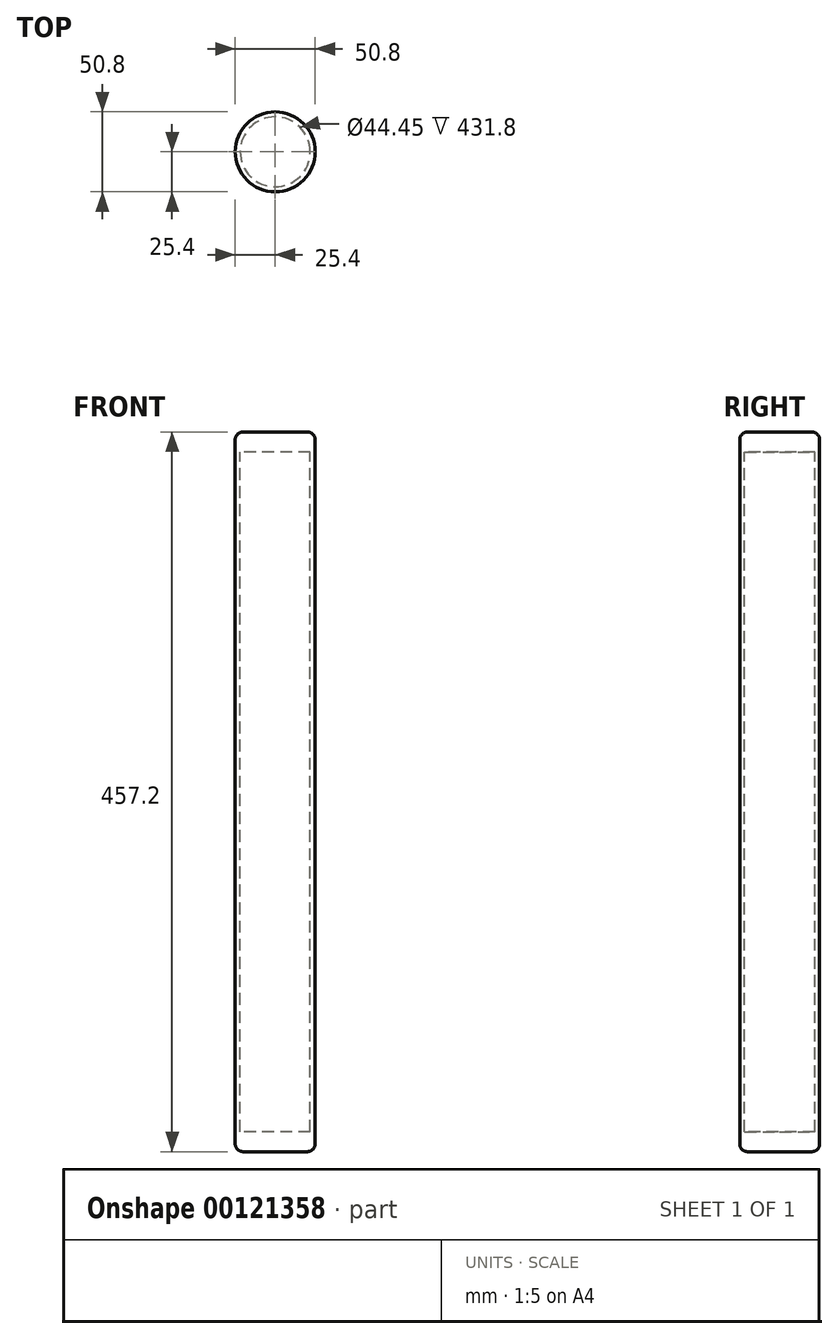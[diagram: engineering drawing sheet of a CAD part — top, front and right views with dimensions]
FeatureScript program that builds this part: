
annotation { "Feature Type Name" : "Feature", "Feature Type Description" : "" }
export const myFeature = defineFeature(function(context is Context, id is Id, definition is map)
    precondition{}
    {
        {
            var Q0;
            Q0=qCreatedBy(makeId("Top.planeOp"),FACE);
            var sketch = newSketch(context, id + "F0", { "sketchPlane" : qUnion([Q0])});
            skCircle(sketch, "E0", {"center": v(0, 0) * mm, "radius": 25.4 * mm});
            skSolve(sketch);
        }
        {
            var Q0;
            Q0 = qSketchRegion(id + "F0", true);
            extrude(context, id + "F1", {"entities" : qUnion([Q0]), "depth" : 444.5 * mm});
        }
        {
            var Q0;
            Q0=makeQuery(id+"F1.opExtrude","CAP_FACE",FACE,{"disambiguationData":[OSD([sQuery(id+"F0.wireOp",EDGE,"E0")])],"isStart":false});
            var sketch = newSketch(context, id + "F2", { "sketchPlane" : qUnion([Q0])});
            skCircle(sketch, "E1", {"center": v(0, 0) * mm, "radius": 22.23 * mm});
            skSolve(sketch);
        }
        {
            var Q0;
            Q0 = qSketchRegion(id + "F2", true);
            extrude(context, id + "F3", {"entities" : qUnion([Q0]), "operationType" : NewBodyOperationType.REMOVE, "oppositeDirection" : true, "depth" : 431.8 * mm});
        }
        {
            var Q0;
            Q0=makeQuery(id+"F1.opExtrude","CAP_FACE",FACE,{"disambiguationData":[OSD([sQuery(id+"F0.wireOp",EDGE,"E0")])],"isStart":false});
            var sketch = newSketch(context, id + "F4", { "sketchPlane" : qUnion([Q0])});
            skCircle(sketch, "E2", {"center": v(0, 0) * mm, "radius": 25.4 * mm});
            skSolve(sketch);
        }
        {
            var Q0;
            Q0 = qSketchRegion(id + "F4", true);
            extrude(context, id + "F5", {"entities" : qUnion([Q0]), "operationType" : NewBodyOperationType.ADD, "depth" : 12.7 * mm});
        }
        {
            var Q0;
            Q0=makeQuery(id+"F5.opExtrude","CAP_EDGE",EDGE,{"disambiguationData":[OSD([sQuery(id+"F4.wireOp",EDGE,"E2")])],"isStart":false});
            fillet(context, id + "F6", {"entities" : qUnion([Q0]), "radius" : 5.08 * mm, "tangentPropagation" : true, "allowEdgeOverflow" : false});
        }
        {
            var Q0;
            Q0=makeQuery(id+"F1.opExtrude","CAP_EDGE",EDGE,{"disambiguationData":[OSD([sQuery(id+"F0.wireOp",EDGE,"E0")])],"isStart":true});
            fillet(context, id + "F7", {"entities" : qUnion([Q0]), "radius" : 5.08 * mm, "tangentPropagation" : true, "allowEdgeOverflow" : false});
        }
    });
